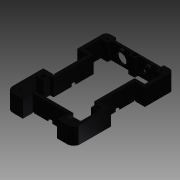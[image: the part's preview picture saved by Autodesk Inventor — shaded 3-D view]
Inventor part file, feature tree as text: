
AUTODESK INVENTOR PART (.ipt)
format: ipt  version: 2015 (Build 190159000, 159)  size: 614,400 bytes
history: native  units: mm
features: extrude x12, sketch x12, fillet x4, hole x3
ambient origin geometry x8: Origin, YZ Plane, XZ Plane, XY Plane, X Axis, Y Axis, Z Axis, Center Point
bodies: Volumenkörper1 (feature_tree)
feature tree (31):
  extrude  "Extrusion1"  Depth=100.0mm
  fillet  "Rundung2"  Radius=24.5mm
  fillet  "Rundung3"  Radius=10.0mm
  extrude  "Extrusion2"  Depth=3.5mm
  extrude  "Extrusion11"  Depth=3.5mm
  fillet  "Rundung8"  Radius=3.5mm
  fillet  "Rundung9"  Radius=3.5mm
  extrude  "Extrusion12"  Depth=3.5mm
  hole  "Bohrung2"  [1 undecoded]
  hole  "Bohrung3"  [1 undecoded]
  hole  "Bohrung4"  [1 undecoded]
  extrude  "Extrusion13"  Depth=100.0mm
  extrude  "Extrusion20"  Depth=60.0mm
  extrude  "Extrusion14"  Depth=10.0mm
  extrude  "Extrusion15"  Depth=10.0mm
  extrude  "Extrusion16"  Depth=90.0mm
  extrude  "Extrusion17"  Depth=70.0mm
  extrude  "Extrusion21"  Depth=30.0mm
  extrude  "Extrusion22"  Depth=10.0mm
  sketch  "Skizze1"  dims[d0=145.0mm d1=100.0mm d2=24.5mm d3=0.0mm d10=10.0mm]
  sketch  "Skizze3"  dims[d11=5.0mm d12=3.5mm]
  sketch  "Skizze10"  dims[d13=3.5mm d14=3.5mm d15=3.5mm d16=3.5mm]
  sketch  "Skizze11"  dims[d17=3.5mm d18=3.5mm]
  sketch  "Skizze12"  dims[d19=3.5mm d20=3.5mm]
  sketch  "Skizze13"  dims[d21=3.5mm d22=3.5mm]
  sketch  "Skizze14"  dims[d23=140.0mm d24=140.0mm]
  sketch  "Skizze15"  dims[d25=140.0mm d26=100.0mm]
  sketch  "Skizze16"  dims[d27=100.0mm d28=60.0mm]
  sketch  "Skizze17"  dims[d29=60.0mm d30=10.0mm]
  sketch  "Skizze18"  dims[d31=10.0mm d32=10.0mm]
  sketch  "Skizze19"  dims[d33=10.0mm d34=90.0mm d35=70.0mm d36=30.0mm d37=10.0mm d38=90.0mm d39=10.0mm d40=90.0mm d41=10.0mm d42=90.0mm d43=50.0mm d44=10.0mm d45=6.0mm d46=0.0mm d120=10.0mm d121=10.0mm d125=10.1mm d128=10.0mm d129=10.0mm d130=10.0mm d131=5.0mm d132=5.0mm d133=10.0mm d134=30.0mm d135=30.0mm d137=5.0mm d138=5.0mm d139=25.0mm d140=25.0mm d141=5.0mm d142=5.0mm d143=5.0mm d144=5.0mm d145=60.0mm d146=60.0mm d149=5.0mm d150=10.0mm d152=4.0mm d154=4.0mm d155=4.0mm d158=5.0mm d159=15.0mm d160=15.1mm d161=15.1mm d162=15.1mm d163=50.1mm d164=15.1mm d165=50.1mm d166=4.95mm d167=4.95mm d168=15.1mm d170=50.0mm d171=50.1mm d172=4.95mm d173=5.05mm d177=10.0mm d178=10.0mm d179=10.0mm d180=10.0mm d181=3.5mm d182=3.5mm d183=45.0mm d184=45.0mm d185=10.0mm d186=10.0mm d187=10.0mm d188=0.0mm d189=1.0mm d190=1.0mm d191=10.0mm d192=10.0mm d193=15.5mm d194=3.3mm d195=3.3mm d196=22.5mm d197=11.25mm d200=2.2mm d202=7.0mm d203=5.0mm d212=9.0mm d213=3.0mm d215=4.5mm d216=5.0mm d217=2.2mm d219=5.0mm d220=4.5mm d221=9.0mm d222=2.75mm d223=1.75mm d224=2.25mm d225=2.25mm d226=2.25mm d227=2.25mm d228=5.0mm d229=5.0mm d230=5.0mm d231=8.0mm d232=21.0mm d233=10.0mm d234=0.0mm d235=9.0mm d236=9.0mm d237=9.0mm d238=9.0mm d239=10.0mm d240=45.0mm d241=3.4mm d242=6.0mm d243=6.5mm d244=4.0mm d245=90.0deg d246=8.0mm d247=20.594885mm d248=10.0mm d249=45.0mm d250=3.4mm d251=6.0mm d252=6.5mm d253=4.0mm d254=90.0deg d255=8.0mm d256=20.594885mm d257=140.0mm d258=50.0mm d259=3.4mm d260=6.0mm d261=6.5mm d262=4.0mm d263=90.0deg d264=8.0mm d265=20.594885mm d266=8.0mm d267=8.0mm d268=8.0mm d269=3.8mm d270=3.8mm d271=3.8mm d272=0.5mm d273=0.5mm d274=0.5mm d275=21.2mm d276=21.2mm d277=21.0mm d278=6.0mm d279=0.0mm d280=1.0mm d281=1.0mm d282=1.0mm d283=1.0mm d284=1.0mm d285=1.0mm d286=0.81mm d287=0.81mm d288=0.81mm d289=0.81mm d290=1.54mm d291=1.84mm d292=1.54mm d293=1.84mm d294=0.81mm d295=0.81mm d296=0.81mm d297=0.81mm d298=1.54mm d299=1.54mm d300=1.0mm d301=1.0mm d302=1.0mm d303=1.0mm d304=1.0mm d305=1.0mm d306=1.84mm d307=1.84mm d308=0.81mm d309=0.81mm d310=0.81mm d311=0.81mm d312=1.0mm d313=1.0mm d314=1.0mm d315=1.0mm d317=1.0mm d318=1.54mm d320=1.0mm d321=1.54mm d322=1.84mm d323=1.84mm d324=4.0mm d325=0.0mm d326=1.0mm d327=0.0mm d331=0.8mm d333=0.8mm d334=4.0mm d335=0.0mm d336=0.8mm d337=0.8mm d338=4.0mm d339=0.0mm d340=6.1mm d341=6.1mm d342=0.05mm d343=0.05mm d344=0.1mm d345=0.1mm d347=0.05mm d348=0.05mm d349=0.05mm d350=0.05mm d351=0.1mm d356=30.0mm d357=0.0mm d358=2.0mm d359=2.0mm d360=2.0mm d361=2.0mm d362=2.0mm d363=2.0mm d364=30.0mm d365=0.0mm d366=0.3mm d367=0.3mm d368=0.3mm d369=0.3mm d370=6.0mm d371=0.0mm d372=0.0mm d377=4.5mm d378=4.5mm]
note: 3 required parameter values undecoded (feature->parameter linkage not recoverable at this tier; creation-order binding heuristic only, values carry confidence <= 0.55)
